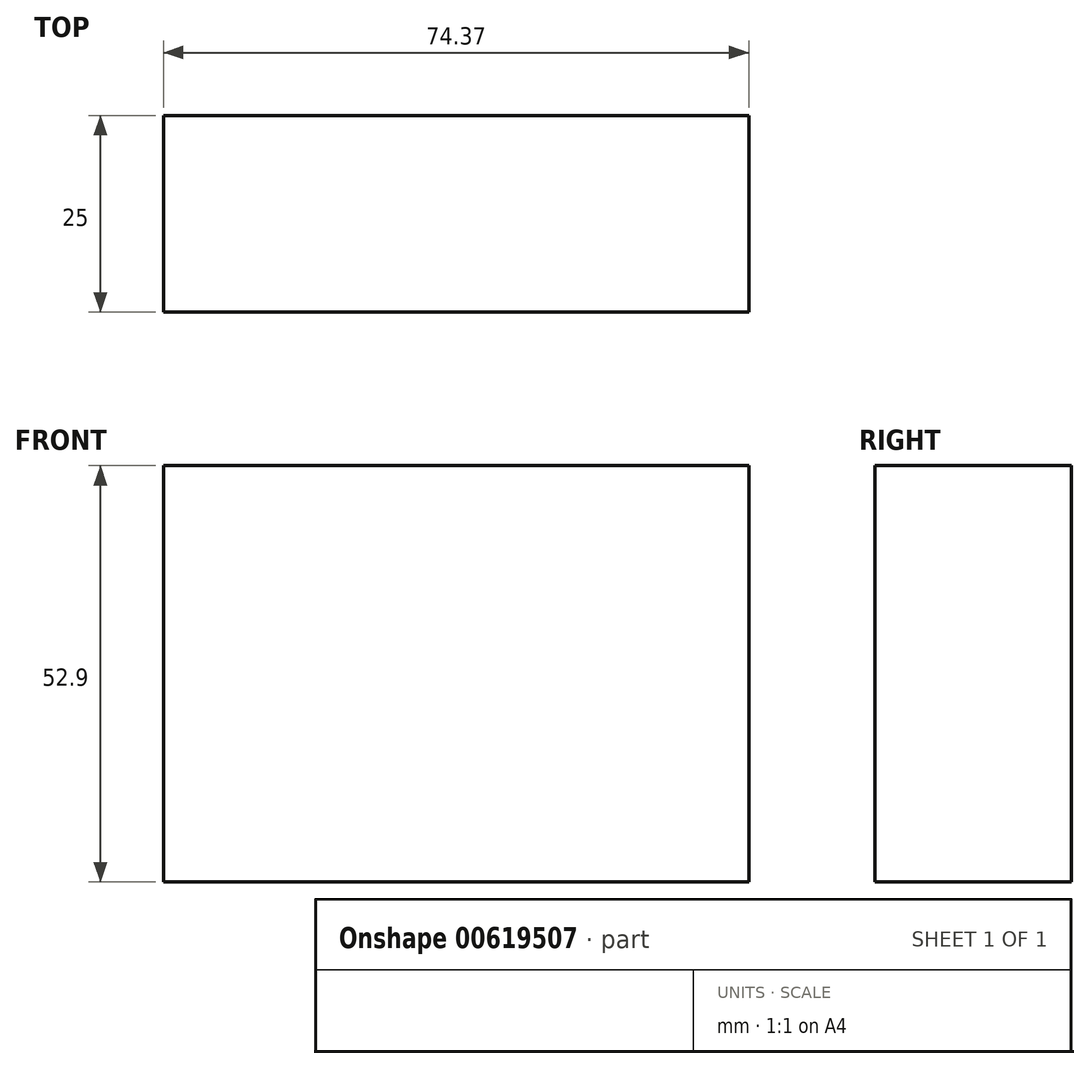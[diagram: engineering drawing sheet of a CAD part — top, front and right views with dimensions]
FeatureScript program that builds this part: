
annotation { "Feature Type Name" : "Feature", "Feature Type Description" : "" }
export const myFeature = defineFeature(function(context is Context, id is Id, definition is map)
    precondition{}
    {
        {
            var Q0;
            Q0=qCreatedBy(makeId("Front.planeOp"),FACE);
            var sketch = newSketch(context, id + "F0", { "sketchPlane" : qUnion([Q0])});
            skLineSegment(sketch, "E0.bottom", {"start": v(-129.46, 39.7) * mm, "end": v(-55.1, 39.7) * mm});
            skLineSegment(sketch, "E0.top", {"start": v(-129.46, -13.2) * mm, "end": v(-55.1, -13.2) * mm});
            skLineSegment(sketch, "E0.left", {"start": v(-129.46, 39.7) * mm, "end": v(-129.46, -13.2) * mm});
            skLineSegment(sketch, "E0.right", {"start": v(-55.1, 39.7) * mm, "end": v(-55.1, -13.2) * mm});
            skSolve(sketch);
        }
        {
            var Q0;
            Q0 = qSketchRegion(id + "F0", true);
            extrude(context, id + "F1", {"entities" : qUnion([Q0]), "depth" : 25 * mm, "offsetDistance" : 25 * mm});
        }
    });
